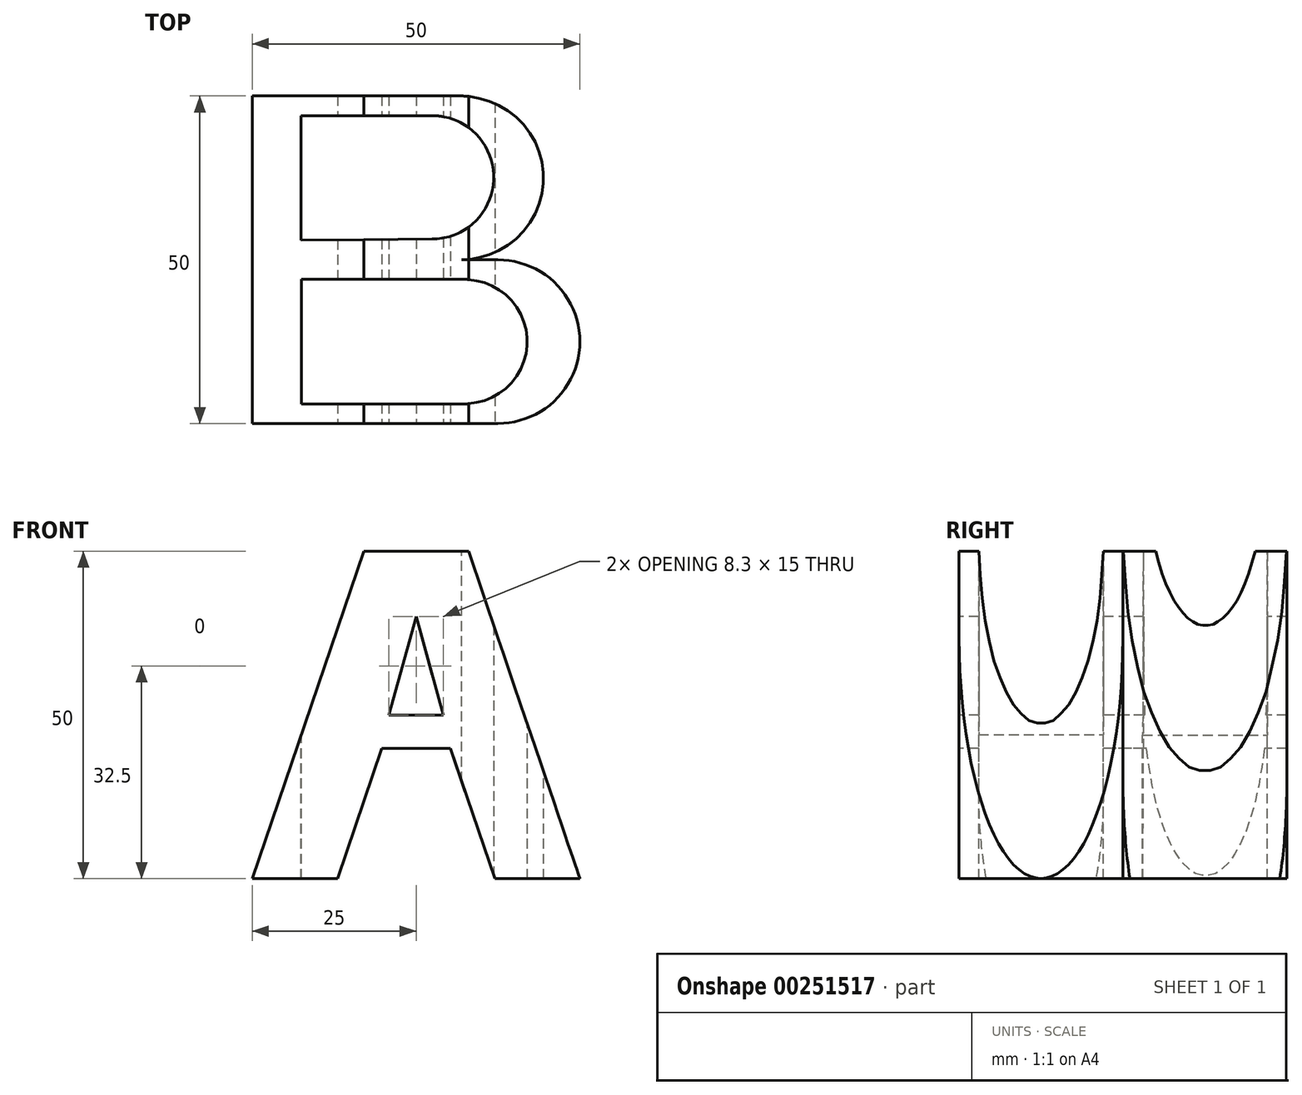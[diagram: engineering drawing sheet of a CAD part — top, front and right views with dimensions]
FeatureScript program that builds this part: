
annotation { "Feature Type Name" : "Feature", "Feature Type Description" : "" }
export const myFeature = defineFeature(function(context is Context, id is Id, definition is map)
    precondition{}
    {
        {
            var Q0;
            Q0=qCreatedBy(makeId("Front.planeOp"),FACE);
            var sketch = newSketch(context, id + "F0", { "sketchPlane" : qUnion([Q0])});
            skLineSegment(sketch, "E0.bottom", {"start": v(25, 25) * mm, "end": v(-25, 25) * mm});
            skLineSegment(sketch, "E0.top", {"start": v(25, -25) * mm, "end": v(-25, -25) * mm});
            skLineSegment(sketch, "E0.left", {"start": v(25, 25) * mm, "end": v(25, -25) * mm});
            skLineSegment(sketch, "E0.right", {"start": v(-25, 25) * mm, "end": v(-25, -25) * mm});
            skPoint(sketch, "E0.middle", {"position": v(0, 0) * mm});
            skSolve(sketch);
        }
        {
            var Q0;
            Q0=makeQuery(id+"F0.imprint","IMPRINT",FACE,{"disambiguationData":[TD([[makeQuery(id+"F0.imprint","IMPRINT",EDGE,{"derivedFrom":sQuery(id+"F0.wireOp",EDGE,"E0.bottom")}),1.0]])]});
            extrude(context, id + "F1", {"entities" : qUnion([Q0]), "endBound" : BoundingType.SYMMETRIC, "depth" : 50 * mm});
        }
        {
            var Q0;
            Q0=makeQuery(id+"F1.opExtrude","CAP_FACE",FACE,{"disambiguationData":[OSD([sQuery(id+"F0.wireOp",EDGE,"E0.bottom"),sQuery(id+"F0.wireOp",EDGE,"E0.top"),sQuery(id+"F0.wireOp",EDGE,"E0.left"),sQuery(id+"F0.wireOp",EDGE,"E0.right")])],"isStart":false});
            cPlane(context, id + "F2", {"entities" : qUnion([Q0]), "cplaneType" : CPlaneType.OFFSET, "offset" : 0 * mm, "width" : 150 * mm, "height" : 150 * mm});
        }
        {
            var Q0;
            Q0=qCreatedBy(id+"F2.planeOp",FACE);
            var sketch = newSketch(context, id + "F3", { "sketchPlane" : qUnion([Q0])});
            skLineSegment(sketch, "E1", {"start": v(-25, 25) * mm, "end": v(-8, 25) * mm});
            skLineSegment(sketch, "E2", {"start": v(25, 25) * mm, "end": v(8, 25) * mm});
            skLineSegment(sketch, "E3", {"start": v(-25, -25) * mm, "end": v(-12, -25) * mm});
            skLineSegment(sketch, "E4", {"start": v(25, -25) * mm, "end": v(12, -25) * mm});
            skLineSegment(sketch, "E5", {"start": v(-25, -25) * mm, "end": v(-8, 25) * mm});
            skLineSegment(sketch, "E6", {"start": v(8, 25) * mm, "end": v(25, -25) * mm});
            skPoint(sketch, "E7.endSnap0", {"position": v(16.5, 0) * mm});
            skLineSegment(sketch, "E8", {"start": v(-5.24, -5.12) * mm, "end": v(-12, -25) * mm});
            skLineSegment(sketch, "E9", {"start": v(5.24, -5.12) * mm, "end": v(12, -25) * mm});
            skLineSegment(sketch, "E10", {"start": v(-5.24, -5.12) * mm, "end": v(5.24, -5.12) * mm});
            skLineSegment(sketch, "E11", {"start": v(0, 15) * mm, "end": v(-4.15, 0) * mm});
            skLineSegment(sketch, "E12", {"start": v(-4.15, 0) * mm, "end": v(0, 0) * mm});
            skLineSegment(sketch, "E13", {"start": v(0, 0) * mm, "end": v(4.15, 0) * mm});
            skLineSegment(sketch, "E14", {"start": v(4.15, 0) * mm, "end": v(0, 15) * mm});
            skLineSegment(sketch, "E15", {"start": v(-12, -25) * mm, "end": v(12, -25) * mm});
            skLineSegment(sketch, "E16", {"start": v(-25, -25) * mm, "end": v(-25, 25) * mm});
            skLineSegment(sketch, "E17", {"start": v(25, 25) * mm, "end": v(25, -25) * mm});
            skSolve(sketch);
        }
        {
            var Q0;
            Q0=makeQuery(id+"F3.imprint","IMPRINT",FACE,{"disambiguationData":[TD([[makeQuery(id+"F3.imprint","IMPRINT",EDGE,{"derivedFrom":sQuery(id+"F3.wireOp",EDGE,"E1")}),-1.0]])]});
            var Q1;
            Q1=makeQuery(id+"F3.imprint","IMPRINT",FACE,{"disambiguationData":[TD([[makeQuery(id+"F3.imprint","IMPRINT",EDGE,{"derivedFrom":sQuery(id+"F3.wireOp",EDGE,"E11")}),1.0]])]});
            var Q2;
            Q2=makeQuery(id+"F3.imprint","IMPRINT",FACE,{"disambiguationData":[TD([[makeQuery(id+"F3.imprint","IMPRINT",EDGE,{"derivedFrom":sQuery(id+"F3.wireOp",EDGE,"E2")}),1.0]])]});
            var Q3;
            Q3=makeQuery(id+"F3.imprint","IMPRINT",FACE,{"disambiguationData":[TD([[makeQuery(id+"F3.imprint","IMPRINT",EDGE,{"derivedFrom":sQuery(id+"F3.wireOp",EDGE,"E8")}),1.0]])]});
            extrude(context, id + "F4", {"entities" : qUnion([Q0, Q1, Q2, Q3]), "operationType" : NewBodyOperationType.REMOVE, "oppositeDirection" : true, "depth" : 50 * mm});
        }
        {
            var Q0;
            Q0=makeQuery(id+"F1.opExtrude","SWEPT_FACE",FACE,{"disambiguationData":[OSD([sQuery(id+"F0.wireOp",EDGE,"E0.bottom")])]});
            cPlane(context, id + "F5", {"entities" : qUnion([Q0]), "cplaneType" : CPlaneType.OFFSET, "offset" : 0 * mm, "width" : 150 * mm, "height" : 150 * mm});
        }
        {
            var Q0;
            Q0=qCreatedBy(id+"F5.planeOp",FACE);
            var sketch = newSketch(context, id + "F6", { "sketchPlane" : qUnion([Q0])});
            skLineSegment(sketch, "E18", {"start": v(-25, 25) * mm, "end": v(-25, -25) * mm});
            skLineSegment(sketch, "E19", {"start": v(25, -25) * mm, "end": v(12.5, -25) * mm});
            skArc(sketch, "E20", {"start": v(12.5, -25) * mm, "mid": v(25, -12.5) * mm, "end": v(12.5, 0) * mm});
            skLineSegment(sketch, "E21", {"start": v(25, -25) * mm, "end": v(25, 25) * mm});
            skLineSegment(sketch, "E22", {"start": v(25, 25) * mm, "end": v(-25, 25) * mm});
            skLineSegment(sketch, "E23", {"start": v(-25, -25) * mm, "end": v(12.5, -25) * mm});
            skPoint(sketch, "E24.endSnap0", {"position": v(-25, 0) * mm});
            skLineSegment(sketch, "E25", {"start": v(-17.54, 22) * mm, "end": v(-17.54, 3) * mm});
            skLineSegment(sketch, "E26", {"start": v(-17.54, 22) * mm, "end": v(2.46, 22) * mm});
            skLineSegment(sketch, "E27", {"start": v(12.5, 0) * mm, "end": v(7.5, 0) * mm});
            skArc(sketch, "E28", {"start": v(6.96, 25) * mm, "mid": v(19.46, 12.5) * mm, "end": v(6.96, 0) * mm});
            skLineSegment(sketch, "E29", {"start": v(-17.51, -3) * mm, "end": v(-17.51, -22) * mm});
            skLineSegment(sketch, "E30", {"start": v(-17.51, -3) * mm, "end": v(7.49, -3) * mm});
            skLineSegment(sketch, "E31", {"start": v(-17.54, 3) * mm, "end": v(2.46, 3.17) * mm});
            skLineSegment(sketch, "E32", {"start": v(-17.51, -22) * mm, "end": v(7.49, -22) * mm});
            skArc(sketch, "E33", {"start": v(2.46, 22) * mm, "mid": v(11.87, 12.59) * mm, "end": v(2.46, 3.17) * mm});
            skArc(sketch, "E34", {"start": v(7.49, -3) * mm, "mid": v(16.99, -12.5) * mm, "end": v(7.49, -22) * mm});
            skLineSegment(sketch, "E35", {"start": v(-25, 25) * mm, "end": v(6.96, 25) * mm});
            skLineSegment(sketch, "E36", {"start": v(6.96, 25) * mm, "end": v(25, 25) * mm});
            skLineSegment(sketch, "E37", {"start": v(25, 25) * mm, "end": v(25, -25) * mm});
            skLineSegment(sketch, "E38", {"start": v(6.96, 0) * mm, "end": v(7.5, 0) * mm});
            skSolve(sketch);
        }
        {
            var Q0;
            {var subQ4=sQuery(id+"F6.wireOp",EDGE,"E27");Q0=makeQuery(id+"F6.imprint","IMPRINT",FACE,{"disambiguationData":[TD([[makeQuery(id+"F6.imprint","IMPRINT",EDGE,{"derivedFrom":subQ4}),-1.0]])]});}
            var Q1;
            {var subQ0=sQuery(id+"F6.wireOp",EDGE,"E19");Q1=makeQuery(id+"F6.imprint","IMPRINT",FACE,{"disambiguationData":[TD([[makeQuery(id+"F6.imprint","IMPRINT",EDGE,{"derivedFrom":subQ0}),-1.0]])]});}
            var Q2;
            Q2=makeQuery(id+"F6.imprint","IMPRINT",FACE,{"disambiguationData":[TD([[makeQuery(id+"F6.imprint","IMPRINT",EDGE,{"derivedFrom":sQuery(id+"F6.wireOp",EDGE,"E29")}),1.0]])]});
            var Q3;
            Q3=makeQuery(id+"F6.imprint","IMPRINT",FACE,{"disambiguationData":[TD([[makeQuery(id+"F6.imprint","IMPRINT",EDGE,{"derivedFrom":sQuery(id+"F6.wireOp",EDGE,"E25")}),1.0]])]});
            extrude(context, id + "F7", {"entities" : qUnion([Q0, Q1, Q2, Q3]), "operationType" : NewBodyOperationType.REMOVE, "oppositeDirection" : true, "depth" : 50 * mm});
        }
    });
